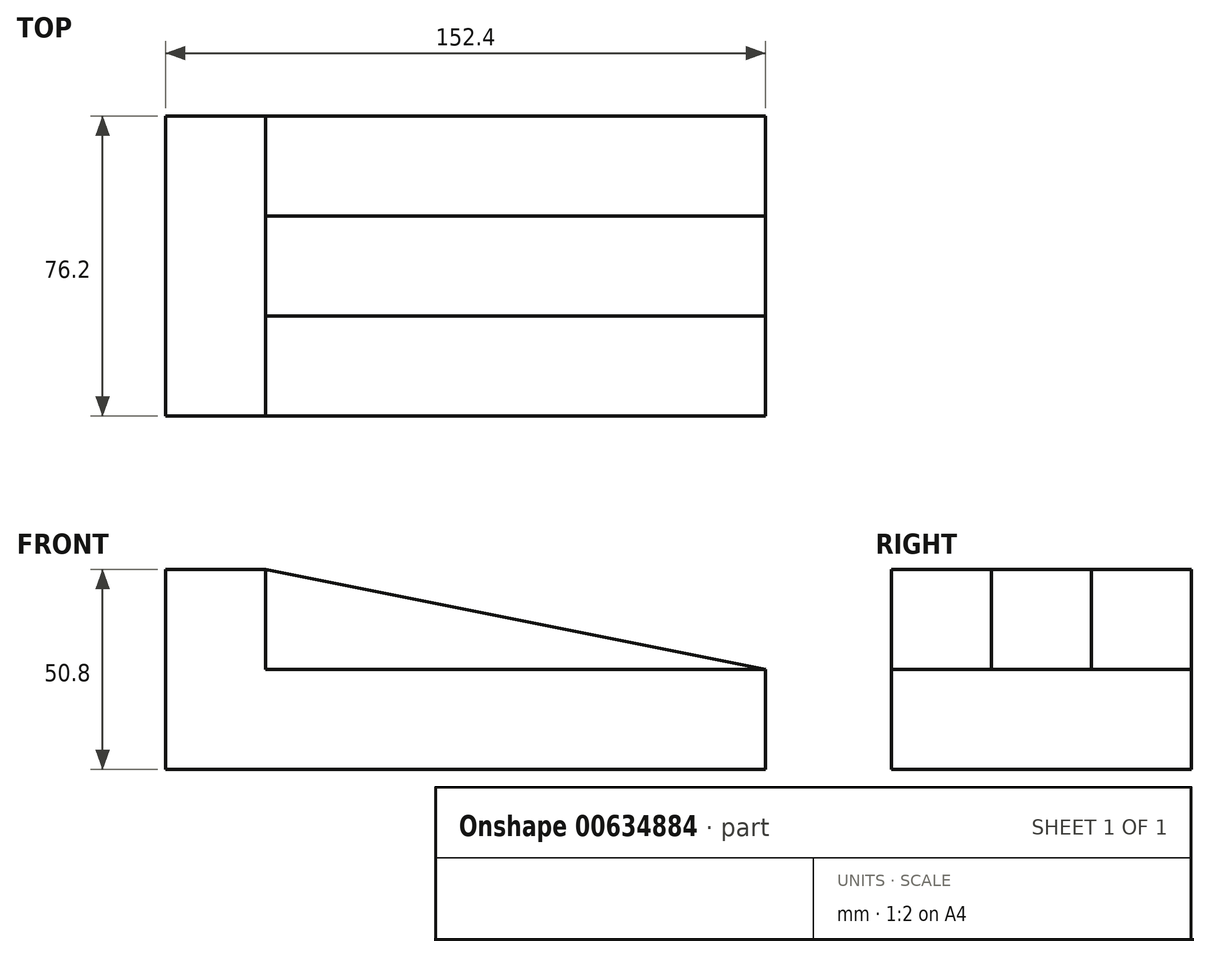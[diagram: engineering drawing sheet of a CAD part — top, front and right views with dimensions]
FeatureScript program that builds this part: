
annotation { "Feature Type Name" : "Feature", "Feature Type Description" : "" }
export const myFeature = defineFeature(function(context is Context, id is Id, definition is map)
    precondition{}
    {
        {
            var Q0;
            Q0=qCreatedBy(makeId("Front.planeOp"),FACE);
            var sketch = newSketch(context, id + "F0", { "sketchPlane" : qUnion([Q0])});
            skLineSegment(sketch, "E0", {"start": v(-86.94, 32.47) * mm, "end": v(-86.94, -18.33) * mm});
            skLineSegment(sketch, "E1", {"start": v(-86.94, -18.33) * mm, "end": v(65.46, -18.33) * mm});
            skLineSegment(sketch, "E2", {"start": v(65.46, -18.33) * mm, "end": v(65.46, 7.07) * mm});
            skLineSegment(sketch, "E3", {"start": v(65.46, 7.07) * mm, "end": v(-61.54, 7.07) * mm});
            skLineSegment(sketch, "E4", {"start": v(-61.54, 7.07) * mm, "end": v(-61.54, 32.47) * mm});
            skLineSegment(sketch, "E5", {"start": v(-61.54, 32.47) * mm, "end": v(-86.94, 32.47) * mm});
            skLineSegment(sketch, "E6", {"start": v(65.46, 7.07) * mm, "end": v(-61.54, 32.47) * mm});
            skSolve(sketch);
        }
        {
            var Q0;
            Q0=makeQuery(id+"F0.imprint","IMPRINT",FACE,{"disambiguationData":[TD([[makeQuery(id+"F0.imprint","IMPRINT",EDGE,{"derivedFrom":sQuery(id+"F0.wireOp",EDGE,"E0")}),1.0]])]});
            extrude(context, id + "F1", {"entities" : qUnion([Q0]), "oppositeDirection" : true, "depth" : 50.8 * mm, "offsetDistance" : 25.4 * mm});
        }
        {
            var Q0;
            Q0=makeQuery(id+"F0.imprint","IMPRINT",FACE,{"disambiguationData":[TD([[makeQuery(id+"F0.imprint","IMPRINT",EDGE,{"derivedFrom":sQuery(id+"F0.wireOp",EDGE,"E0")}),1.0]])]});
            extrude(context, id + "F2", {"entities" : qUnion([Q0]), "operationType" : NewBodyOperationType.ADD, "depth" : 25.4 * mm, "offsetDistance" : 25.4 * mm});
        }
        {
            var Q0;
            Q0=makeQuery(id+"F0.imprint","IMPRINT",FACE,{"disambiguationData":[TD([[makeQuery(id+"F0.imprint","IMPRINT",EDGE,{"derivedFrom":sQuery(id+"F0.wireOp",EDGE,"E3")}),-1.0]])]});
            extrude(context, id + "F3", {"entities" : qUnion([Q0]), "operationType" : NewBodyOperationType.ADD, "oppositeDirection" : true, "depth" : 25.4 * mm, "offsetDistance" : 25.4 * mm});
        }
    });
